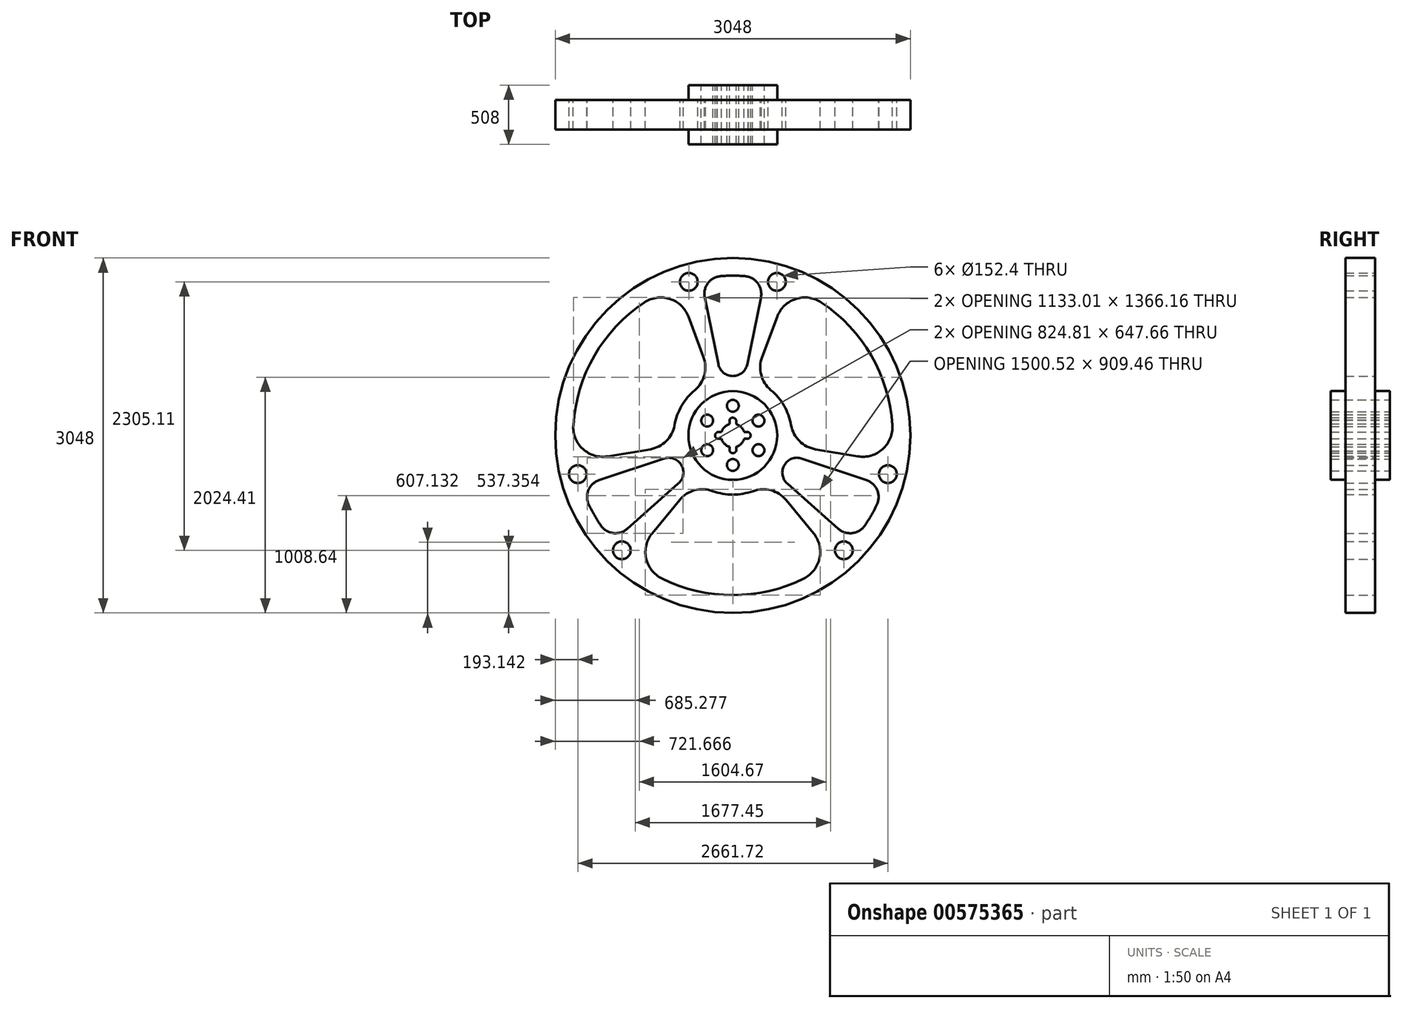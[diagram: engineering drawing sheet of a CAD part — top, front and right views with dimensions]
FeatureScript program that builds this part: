
annotation { "Feature Type Name" : "Feature", "Feature Type Description" : "" }
export const myFeature = defineFeature(function(context is Context, id is Id, definition is map)
    precondition{}
    {
        {
            var Q0;
            Q0=qCreatedBy(makeId("Front.planeOp"),FACE);
            var sketch = newSketch(context, id + "F0", { "sketchPlane" : qUnion([Q0])});
            skCircle(sketch, "E0", {"center": v(0, 0) * mm, "radius": 1524 * mm});
            skCircle(sketch, "E1", {"center": v(-378.06, 1318.47) * mm, "radius": 76.2 * mm});
            skCircle(sketch, "E2", {"center": v(378.06, 1318.47) * mm, "radius": 76.2 * mm});
            skCircle(sketch, "E3.1.0", {"center": v(-952.8, -986.65) * mm, "radius": 76.2 * mm});
            skCircle(sketch, "E3.1.1", {"center": v(-1330.86, -331.82) * mm, "radius": 76.2 * mm});
            skCircle(sketch, "E3.2.0", {"center": v(1330.86, -331.82) * mm, "radius": 76.2 * mm});
            skCircle(sketch, "E3.2.1", {"center": v(952.8, -986.65) * mm, "radius": 76.2 * mm});
            skLineSegment(sketch, "E4", {"start": v(251.6, 672.92) * mm, "end": v(381.15, 1019.43) * mm});
            skLineSegment(sketch, "E5", {"start": v(708.57, -118.57) * mm, "end": v(1073.43, -179.63) * mm});
            skLineSegment(sketch, "E6.2.0", {"start": v(456.97, -554.35) * mm, "end": v(692.28, -839.8) * mm});
            skLineSegment(sketch, "E6.2.1", {"start": v(-456.97, -554.35) * mm, "end": v(-692.28, -839.8) * mm});
            skPoint(sketch, "E7.orphan", {"position": v(-903.17, 2415.63) * mm});
            skPoint(sketch, "E8.orphan", {"position": v(706, 1888.26) * mm});
            skPoint(sketch, "E9.orphan", {"position": v(2543.58, -425.65) * mm});
            skPoint(sketch, "E10.orphan", {"position": v(1282.29, -1555.54) * mm});
            skPoint(sketch, "E11.orphan", {"position": v(-1640.41, -1989.98) * mm});
            skPoint(sketch, "E12.orphan", {"position": v(-1988.28, -332.72) * mm});
            skArc(sketch, "E13.trimOffspring", {"start": v(-759.76, 1141.95) * mm, "mid": v(-1187.84, 685.8) * mm, "end": v(-1368.84, 87) * mm});
            skArc(sketch, "E14.trimOffspring", {"start": v(103.3, 1367.7) * mm, "mid": v(0, 1371.6) * mm, "end": v(-103.3, 1367.7) * mm});
            skArc(sketch, "E15.trimOffspring", {"start": v(1368.84, 87) * mm, "mid": v(1187.84, 685.8) * mm, "end": v(759.76, 1141.95) * mm});
            skArc(sketch, "E16.trimOffspring", {"start": v(-609.08, -1228.95) * mm, "mid": v(0, -1371.6) * mm, "end": v(609.08, -1228.95) * mm});
            skArc(sketch, "E17", {"start": v(-381.15, 1019.43) * mm, "mid": v(-540.86, 1172.14) * mm, "end": v(-759.76, 1141.95) * mm});
            skArc(sketch, "E18", {"start": v(-1368.84, 87) * mm, "mid": v(-1285.53, -117.67) * mm, "end": v(-1073.43, -179.63) * mm});
            skArc(sketch, "E19", {"start": v(-708.57, -118.57) * mm, "mid": v(-571.62, -48.4) * mm, "end": v(-500.33, 87.96) * mm});
            skArc(sketch, "E20", {"start": v(-326.34, 389.31) * mm, "mid": v(-243.9, 519.24) * mm, "end": v(-251.6, 672.92) * mm});
            skLineSegment(sketch, "E21.trimOffspring", {"start": v(-708.57, -118.57) * mm, "end": v(-1073.43, -179.63) * mm});
            skLineSegment(sketch, "E22.trimOffspring", {"start": v(-251.6, 672.92) * mm, "end": v(-381.15, 1019.43) * mm});
            skArc(sketch, "E23.trimOffspring", {"start": v(-326.34, 389.31) * mm, "mid": v(-439.94, 254) * mm, "end": v(-500.33, 87.96) * mm});
            skArc(sketch, "E24.1.1", {"start": v(-692.28, -839.8) * mm, "mid": v(-744.67, -1054.47) * mm, "end": v(-609.08, -1228.95) * mm});
            skArc(sketch, "E24.1.3", {"start": v(-173.99, -477.28) * mm, "mid": v(-327.73, -470.84) * mm, "end": v(-456.97, -554.35) * mm});
            skArc(sketch, "E24.1.4", {"start": v(-173.99, -477.28) * mm, "mid": v(0, -508) * mm, "end": v(173.99, -477.28) * mm});
            skArc(sketch, "E24.1.5", {"start": v(456.97, -554.35) * mm, "mid": v(327.73, -470.84) * mm, "end": v(173.99, -477.28) * mm});
            skArc(sketch, "E24.1.7", {"start": v(609.08, -1228.95) * mm, "mid": v(744.67, -1054.47) * mm, "end": v(692.28, -839.8) * mm});
            skArc(sketch, "E24.2.1", {"start": v(1073.43, -179.63) * mm, "mid": v(1285.53, -117.67) * mm, "end": v(1368.84, 87) * mm});
            skArc(sketch, "E24.2.3", {"start": v(500.33, 87.96) * mm, "mid": v(571.62, -48.4) * mm, "end": v(708.57, -118.57) * mm});
            skArc(sketch, "E24.2.4", {"start": v(500.33, 87.96) * mm, "mid": v(439.94, 254) * mm, "end": v(326.34, 389.31) * mm});
            skArc(sketch, "E24.2.5", {"start": v(251.6, 672.92) * mm, "mid": v(243.9, 519.24) * mm, "end": v(326.34, 389.31) * mm});
            skArc(sketch, "E24.2.7", {"start": v(759.76, 1141.95) * mm, "mid": v(540.86, 1172.14) * mm, "end": v(381.15, 1019.43) * mm});
            skArc(sketch, "E25", {"start": v(241.16, 1185.35) * mm, "mid": v(213.39, 1307.65) * mm, "end": v(103.3, 1367.7) * mm});
            skArc(sketch, "E26", {"start": v(-103.3, 1367.7) * mm, "mid": v(-213.39, 1307.65) * mm, "end": v(-241.16, 1185.35) * mm});
            skArc(sketch, "E27", {"start": v(-124.45, 611.7) * mm, "mid": v(0, 510.01) * mm, "end": v(124.45, 611.7) * mm});
            skLineSegment(sketch, "E28", {"start": v(0, 508) * mm, "end": v(0, 510.01) * mm});
            skPoint(sketch, "E28.endSnap0", {"position": v(0, 1371.6) * mm});
            skLineSegment(sketch, "E29", {"start": v(-124.45, 611.7) * mm, "end": v(-241.16, 1185.35) * mm});
            skLineSegment(sketch, "E30", {"start": v(124.45, 611.7) * mm, "end": v(241.16, 1185.35) * mm});
            skPoint(sketch, "E31.orphan", {"position": v(0, 1750.88) * mm});
            skArc(sketch, "E32.1.0", {"start": v(-1132.82, -773.31) * mm, "mid": v(-1025.76, -838.62) * mm, "end": v(-905.96, -801.53) * mm});
            skArc(sketch, "E32.1.1", {"start": v(-1236.12, -594.4) * mm, "mid": v(-1187.84, -685.8) * mm, "end": v(-1132.82, -773.31) * mm});
            skArc(sketch, "E32.1.2", {"start": v(-1147.13, -383.82) * mm, "mid": v(-1239.15, -469.02) * mm, "end": v(-1236.12, -594.4) * mm});
            skLineSegment(sketch, "E32.1.3", {"start": v(-591.97, -198.07) * mm, "end": v(-1147.13, -383.82) * mm});
            skArc(sketch, "E32.1.4", {"start": v(-467.52, -413.62) * mm, "mid": v(-441.68, -255) * mm, "end": v(-591.97, -198.07) * mm});
            skLineSegment(sketch, "E32.1.5", {"start": v(-467.52, -413.62) * mm, "end": v(-905.96, -801.53) * mm});
            skArc(sketch, "E32.2.0", {"start": v(1236.12, -594.4) * mm, "mid": v(1239.15, -469.02) * mm, "end": v(1147.13, -383.82) * mm});
            skArc(sketch, "E32.2.1", {"start": v(1132.82, -773.31) * mm, "mid": v(1187.84, -685.8) * mm, "end": v(1236.12, -594.4) * mm});
            skArc(sketch, "E32.2.2", {"start": v(905.96, -801.53) * mm, "mid": v(1025.76, -838.62) * mm, "end": v(1132.82, -773.31) * mm});
            skLineSegment(sketch, "E32.2.3", {"start": v(467.52, -413.62) * mm, "end": v(905.96, -801.53) * mm});
            skArc(sketch, "E32.2.4", {"start": v(591.97, -198.07) * mm, "mid": v(441.68, -255) * mm, "end": v(467.52, -413.62) * mm});
            skLineSegment(sketch, "E32.2.5", {"start": v(591.97, -198.07) * mm, "end": v(1147.13, -383.82) * mm});
            skCircle(sketch, "E33", {"center": v(0, 0) * mm, "radius": 381 * mm});
            skArc(sketch, "E34", {"start": v(-28, 97.66) * mm, "mid": v(-71.84, 71.84) * mm, "end": v(-97.66, 28) * mm});
            skCircle(sketch, "E35", {"center": v(0, 254) * mm, "radius": 50.8 * mm});
            skCircle(sketch, "E36.1.0", {"center": v(-219.97, 127) * mm, "radius": 50.8 * mm});
            skCircle(sketch, "E36.2.0", {"center": v(-219.97, -127) * mm, "radius": 50.8 * mm});
            skCircle(sketch, "E36.3.0", {"center": v(0, -254) * mm, "radius": 50.8 * mm});
            skCircle(sketch, "E36.4.0", {"center": v(219.97, -127) * mm, "radius": 50.8 * mm});
            skCircle(sketch, "E36.5.0", {"center": v(219.97, 127) * mm, "radius": 50.8 * mm});
            skArc(sketch, "E37", {"start": v(0, -152.4) * mm, "mid": v(0.33, -152.4) * mm, "end": v(0.67, -152.4) * mm});
            skLineSegment(sketch, "E38", {"start": v(-28, -97.66) * mm, "end": v(-28, -131.8) * mm});
            skLineSegment(sketch, "E39", {"start": v(28, -97.66) * mm, "end": v(28, -134.56) * mm});
            skArc(sketch, "E40", {"start": v(-28, -131.8) * mm, "mid": v(-0.94, -152.36) * mm, "end": v(28, -134.56) * mm});
            skLineSegment(sketch, "E41.1.0", {"start": v(97.66, 28) * mm, "end": v(134.56, 28) * mm});
            skArc(sketch, "E41.1.1", {"start": v(131.8, -28) * mm, "mid": v(152.36, -0.94) * mm, "end": v(134.56, 28) * mm});
            skLineSegment(sketch, "E41.1.2", {"start": v(97.66, -28) * mm, "end": v(131.8, -28) * mm});
            skLineSegment(sketch, "E41.2.0", {"start": v(-28, 97.66) * mm, "end": v(-28, 134.56) * mm});
            skArc(sketch, "E41.2.1", {"start": v(28, 131.8) * mm, "mid": v(0.94, 152.36) * mm, "end": v(-28, 134.56) * mm});
            skLineSegment(sketch, "E41.2.2", {"start": v(28, 97.66) * mm, "end": v(28, 131.8) * mm});
            skLineSegment(sketch, "E41.3.0", {"start": v(-97.66, -28) * mm, "end": v(-134.56, -28) * mm});
            skArc(sketch, "E41.3.1", {"start": v(-131.8, 28) * mm, "mid": v(-152.36, 0.94) * mm, "end": v(-134.56, -28) * mm});
            skLineSegment(sketch, "E41.3.2", {"start": v(-97.66, 28) * mm, "end": v(-131.8, 28) * mm});
            skArc(sketch, "E42.trimOffspring", {"start": v(-97.66, -28) * mm, "mid": v(-71.84, -71.84) * mm, "end": v(-28, -97.66) * mm});
            skArc(sketch, "E43.trimOffspring", {"start": v(28, -97.66) * mm, "mid": v(71.84, -71.84) * mm, "end": v(97.66, -28) * mm});
            skArc(sketch, "E44.trimOffspring", {"start": v(97.66, 28) * mm, "mid": v(71.84, 71.84) * mm, "end": v(28, 97.66) * mm});
            skSolve(sketch);
        }
        {
            var Q0;
            Q0=makeQuery(id+"F0.imprint","IMPRINT",FACE,{"disambiguationData":[TD([[makeQuery(id+"F0.imprint","IMPRINT",EDGE,{"derivedFrom":sQuery(id+"F0.wireOp",EDGE,"E0")}),1.0]])]});
            var Q1;
            Q1=makeQuery(id+"F0.imprint","IMPRINT",FACE,{"disambiguationData":[TD([[makeQuery(id+"F0.imprint","IMPRINT",EDGE,{"derivedFrom":sQuery(id+"F0.wireOp",EDGE,"E33")}),1.0]])]});
            extrude(context, id + "F1", {"entities" : qUnion([Q0, Q1]), "depth" : 254 * mm, "offsetDistance" : 25.4 * mm, "symmetric" : true});
        }
        {
            var Q0;
            Q0=makeQuery(id+"F0.imprint","IMPRINT",FACE,{"disambiguationData":[TD([[makeQuery(id+"F0.imprint","IMPRINT",EDGE,{"derivedFrom":sQuery(id+"F0.wireOp",EDGE,"E33")}),1.0]])]});
            extrude(context, id + "F2", {"entities" : qUnion([Q0]), "operationType" : NewBodyOperationType.ADD, "depth" : 508 * mm, "offsetDistance" : 25.4 * mm, "symmetric" : true});
        }
    });
